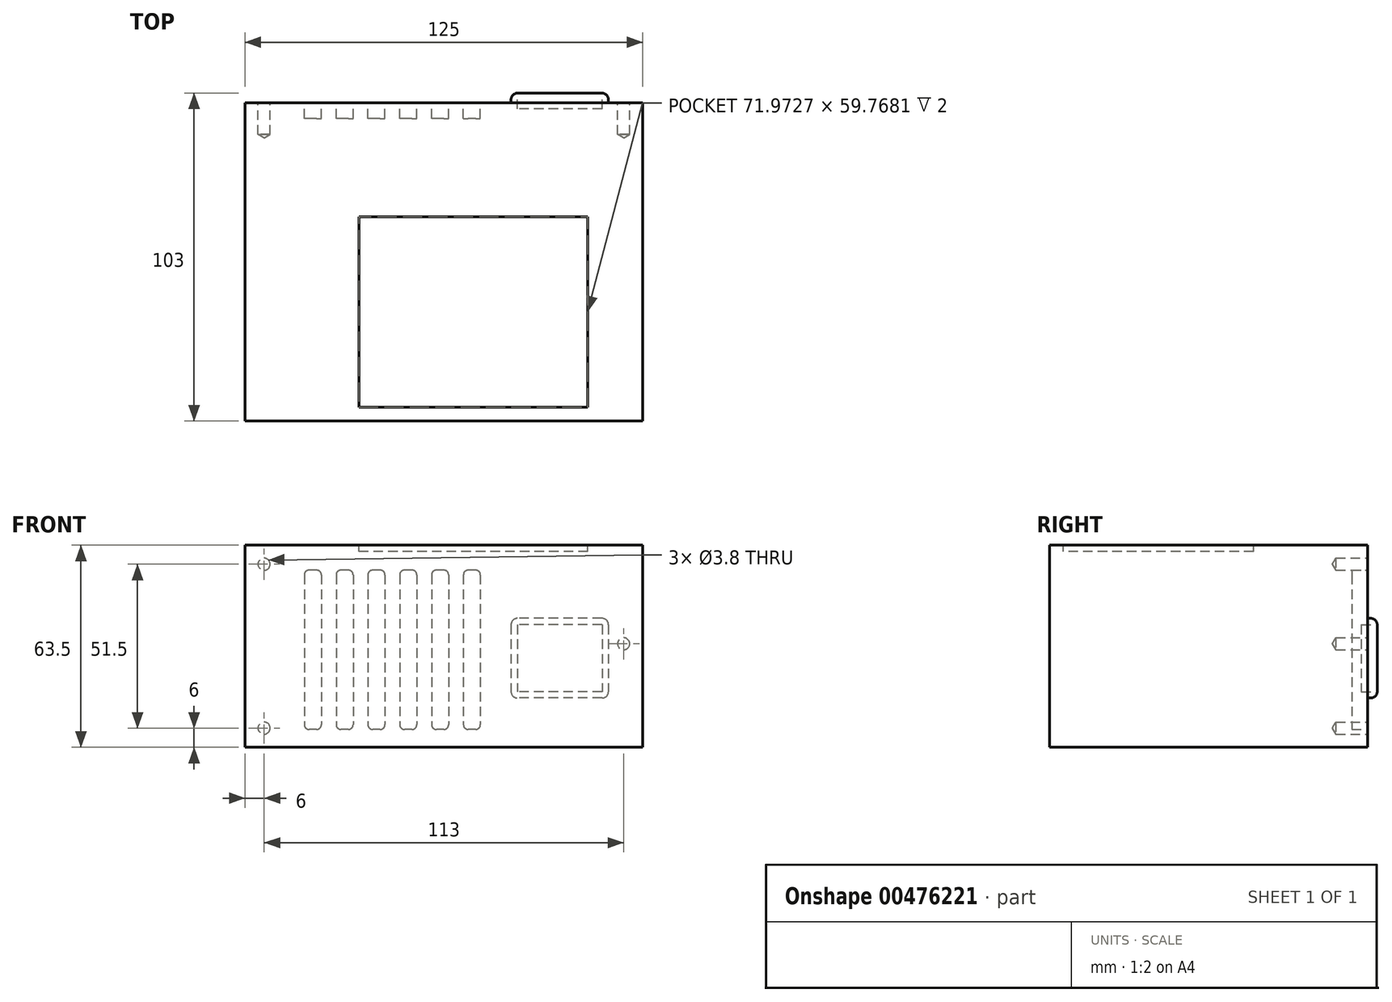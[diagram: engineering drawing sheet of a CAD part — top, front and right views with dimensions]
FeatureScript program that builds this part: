
annotation { "Feature Type Name" : "Feature", "Feature Type Description" : "" }
export const myFeature = defineFeature(function(context is Context, id is Id, definition is map)
    precondition{}
    {
        {
            var Q0;
            Q0=qCreatedBy(makeId("Top.planeOp"),FACE);
            var sketch = newSketch(context, id + "F0", { "sketchPlane" : qUnion([Q0])});
            skLineSegment(sketch, "E0.bottom", {"start": v(62.5, -50) * mm, "end": v(-62.5, -50) * mm});
            skLineSegment(sketch, "E0.top", {"start": v(62.5, 50) * mm, "end": v(-62.5, 50) * mm});
            skLineSegment(sketch, "E0.left", {"start": v(62.5, -50) * mm, "end": v(62.5, 50) * mm});
            skLineSegment(sketch, "E0.right", {"start": v(-62.5, -50) * mm, "end": v(-62.5, 50) * mm});
            skPoint(sketch, "E0.middle", {"position": v(0, 0) * mm});
            skSolve(sketch);
        }
        {
            var Q0;
            Q0=makeQuery(id+"F0.imprint","IMPRINT",FACE,{"disambiguationData":[TD([[makeQuery(id+"F0.imprint","IMPRINT",EDGE,{"derivedFrom":sQuery(id+"F0.wireOp",EDGE,"E0.bottom")}),-1.0]])]});
            extrude(context, id + "F1", {"entities" : qUnion([Q0]), "depth" : 63.5 * mm});
        }
        {
            var Q0;
            Q0=makeQuery(id+"F1.opExtrude","SWEPT_FACE",FACE,{"disambiguationData":[OSD([sQuery(id+"F0.wireOp",EDGE,"E0.top")])]});
            var sketch = newSketch(context, id + "F2", { "sketchPlane" : qUnion([Q0])});
            skPoint(sketch, "E1", {"position": v(56.5, 6) * mm});
            skPoint(sketch, "E2", {"position": v(56.5, 57.5) * mm});
            skPoint(sketch, "E3", {"position": v(-56.5, 32.5) * mm});
            skLineSegment(sketch, "E4.bottom", {"start": v(-51.73, 40.5) * mm, "end": v(-21.11, 40.5) * mm});
            skLineSegment(sketch, "E4.top", {"start": v(-51.73, 15.46) * mm, "end": v(-21.11, 15.46) * mm});
            skLineSegment(sketch, "E4.left", {"start": v(-51.73, 40.5) * mm, "end": v(-51.73, 15.46) * mm});
            skLineSegment(sketch, "E4.right", {"start": v(-21.11, 40.5) * mm, "end": v(-21.11, 15.46) * mm});
            skSolve(sketch);
        }
        {
            var Q0;
            Q0=sQuery(id+"F2.wireOp",VERTEX,"E3");
            var Q1;
            Q1=sQuery(id+"F2.wireOp",VERTEX,"E2");
            var Q2;
            Q2=sQuery(id+"F2.wireOp",VERTEX,"E1");
            var Q3;
            Q3=makeQuery(id+"F1.opExtrude","SWEPT_BODY",BODY,{"disambiguationData":[OSD([sQuery(id+"F0.wireOp",EDGE,"E0.bottom"),sQuery(id+"F0.wireOp",EDGE,"E0.top"),sQuery(id+"F0.wireOp",EDGE,"E0.left"),sQuery(id+"F0.wireOp",EDGE,"E0.right")])]});
            hole(context, id + "F3", {"style" : HoleStyle.SIMPLE, "endStyle" : HoleEndStyle.BLIND, "standardTappedOrClearance" : lookupTablePath({ "standard" : "ANSI", "fit" : "Normal (ASME)", "size" : "#6", "type" : "Clearance" }), "standardBlindInLast" : lookupTablePath({ "fit" : "Free", "standard" : "ANSI", "size" : "#6", "type" : "Clearance" }), "holeDiameter" : 3.8 * mm, "holeDepth" : 10 * mm, "isTappedThrough" : true, "tappedDepth" : 3.8 * mm, "tapClearance" : 0, "locations" : qUnion([Q0, Q1, Q2]), "scope" : qUnion([Q3])});
        }
        {
            var Q0;
            Q0=makeQuery(id+"F2.imprint","IMPRINT",FACE,{"disambiguationData":[TD([[makeQuery(id+"F2.imprint","IMPRINT",EDGE,{"derivedFrom":sQuery(id+"F2.wireOp",EDGE,"E4.bottom")}),-1.0]])]});
            extrude(context, id + "F4", {"entities" : qUnion([Q0]), "operationType" : NewBodyOperationType.ADD, "depth" : 3 * mm});
        }
        {
            var Q0;
            Q0=makeQuery(id+"F4.opExtrude","CAP_FACE",FACE,{"disambiguationData":[OSD([sQuery(id+"F2.wireOp",EDGE,"E4.bottom"),sQuery(id+"F2.wireOp",EDGE,"E4.top"),sQuery(id+"F2.wireOp",EDGE,"E4.left"),sQuery(id+"F2.wireOp",EDGE,"E4.right")])],"isStart":false});
            var Q1;
            Q1=makeQuery(id+"F4.opExtrude","SWEPT_EDGE",EDGE,{"disambiguationData":[OSD([sQuery(id+"F2.wireOp",EDGE,"E4.bottom"),sQuery(id+"F2.wireOp",EDGE,"E4.right")])]});
            var Q2;
            Q2=makeQuery(id+"F4.opExtrude","SWEPT_EDGE",EDGE,{"disambiguationData":[OSD([sQuery(id+"F2.wireOp",EDGE,"E4.top"),sQuery(id+"F2.wireOp",EDGE,"E4.right")])]});
            var Q3;
            Q3=makeQuery(id+"F4.opExtrude","SWEPT_EDGE",EDGE,{"disambiguationData":[OSD([sQuery(id+"F2.wireOp",EDGE,"E4.bottom"),sQuery(id+"F2.wireOp",EDGE,"E4.left")])]});
            var Q4;
            Q4=makeQuery(id+"F4.opExtrude","SWEPT_EDGE",EDGE,{"disambiguationData":[OSD([sQuery(id+"F2.wireOp",EDGE,"E4.top"),sQuery(id+"F2.wireOp",EDGE,"E4.left")])]});
            fillet(context, id + "F5", {"entities" : qUnion([Q0, Q1, Q2, Q3, Q4]), "radius" : 2 * mm, "tangentPropagation" : true, "allowEdgeOverflow" : false});
        }
        {
            var Q0;
            Q0=makeQuery(id+"F1.opExtrude","CAP_FACE",FACE,{"disambiguationData":[OSD([sQuery(id+"F0.wireOp",EDGE,"E0.bottom"),sQuery(id+"F0.wireOp",EDGE,"E0.top"),sQuery(id+"F0.wireOp",EDGE,"E0.left"),sQuery(id+"F0.wireOp",EDGE,"E0.right")])],"isStart":false});
            var sketch = newSketch(context, id + "F6", { "sketchPlane" : qUnion([Q0])});
            skLineSegment(sketch, "E5.bottom", {"start": v(45.26, 14.14) * mm, "end": v(-26.71, 14.14) * mm});
            skLineSegment(sketch, "E5.top", {"start": v(45.26, -45.63) * mm, "end": v(-26.71, -45.63) * mm});
            skLineSegment(sketch, "E5.left", {"start": v(45.26, 14.14) * mm, "end": v(45.26, -45.63) * mm});
            skLineSegment(sketch, "E5.right", {"start": v(-26.71, 14.14) * mm, "end": v(-26.71, -45.63) * mm});
            skSolve(sketch);
        }
        {
            var Q0;
            Q0=makeQuery(id+"F6.imprint","IMPRINT",FACE,{"disambiguationData":[TD([[makeQuery(id+"F6.imprint","IMPRINT",EDGE,{"derivedFrom":sQuery(id+"F6.wireOp",EDGE,"E5.bottom")}),1.0]])]});
            extrude(context, id + "F7", {"entities" : qUnion([Q0]), "operationType" : NewBodyOperationType.REMOVE, "oppositeDirection" : true, "depth" : 2 * mm});
        }
        {
            var Q0;
            Q0=makeQuery(id+"F1.opExtrude","SWEPT_FACE",FACE,{"disambiguationData":[OSD([sQuery(id+"F0.wireOp",EDGE,"E0.top")])]});
            var sketch = newSketch(context, id + "F8", { "sketchPlane" : qUnion([Q0])});
            skLineSegment(sketch, "E6.bottom", {"start": v(-9.99, 55.64) * mm, "end": v(-7.65, 55.64) * mm});
            skLineSegment(sketch, "E6.top", {"start": v(-9.99, 5.58) * mm, "end": v(-7.65, 5.58) * mm});
            skLineSegment(sketch, "E6.left", {"start": v(-11.49, 54.14) * mm, "end": v(-11.49, 7.08) * mm});
            skLineSegment(sketch, "E6.right", {"start": v(-6.15, 54.14) * mm, "end": v(-6.15, 7.08) * mm});
            skPoint(sketch, "E7.visualSharp", {"position": v(-11.49, 55.64) * mm});
            skArc(sketch, "E7.filletArc", {"start": v(-9.99, 55.64) * mm, "mid": v(-11.05, 55.2) * mm, "end": v(-11.49, 54.14) * mm});
            skPoint(sketch, "E8.visualSharp", {"position": v(-6.15, 55.64) * mm});
            skArc(sketch, "E8.filletArc", {"start": v(-6.15, 54.14) * mm, "mid": v(-6.59, 55.2) * mm, "end": v(-7.65, 55.64) * mm});
            skPoint(sketch, "E9.visualSharp", {"position": v(-6.15, 5.58) * mm});
            skArc(sketch, "E9.filletArc", {"start": v(-7.65, 5.58) * mm, "mid": v(-6.59, 6.02) * mm, "end": v(-6.15, 7.08) * mm});
            skPoint(sketch, "E10.visualSharp", {"position": v(-11.49, 5.58) * mm});
            skArc(sketch, "E10.filletArc", {"start": v(-11.49, 7.08) * mm, "mid": v(-11.05, 6.02) * mm, "end": v(-9.99, 5.58) * mm});
            skLineSegment(sketch, "E11.1.0.0", {"start": v(0.01, 55.64) * mm, "end": v(2.35, 55.64) * mm});
            skPoint(sketch, "E11.1.0.1", {"position": v(3.85, 55.64) * mm});
            skArc(sketch, "E11.1.0.2", {"start": v(3.85, 54.14) * mm, "mid": v(3.41, 55.2) * mm, "end": v(2.35, 55.64) * mm});
            skLineSegment(sketch, "E11.1.0.3", {"start": v(3.85, 54.14) * mm, "end": v(3.85, 7.08) * mm});
            skArc(sketch, "E11.1.0.4", {"start": v(2.35, 5.58) * mm, "mid": v(3.41, 6.02) * mm, "end": v(3.85, 7.08) * mm});
            skLineSegment(sketch, "E11.1.0.5", {"start": v(0.01, 5.58) * mm, "end": v(2.35, 5.58) * mm});
            skArc(sketch, "E11.1.0.6", {"start": v(-1.49, 7.08) * mm, "mid": v(-1.05, 6.02) * mm, "end": v(0.01, 5.58) * mm});
            skLineSegment(sketch, "E11.1.0.7", {"start": v(-1.49, 54.14) * mm, "end": v(-1.49, 7.08) * mm});
            skArc(sketch, "E11.1.0.8", {"start": v(0.01, 55.64) * mm, "mid": v(-1.05, 55.2) * mm, "end": v(-1.49, 54.14) * mm});
            skLineSegment(sketch, "E11.2.0.0", {"start": v(10.01, 55.64) * mm, "end": v(12.35, 55.64) * mm});
            skPoint(sketch, "E11.2.0.1", {"position": v(13.85, 55.64) * mm});
            skArc(sketch, "E11.2.0.2", {"start": v(13.85, 54.14) * mm, "mid": v(13.41, 55.2) * mm, "end": v(12.35, 55.64) * mm});
            skLineSegment(sketch, "E11.2.0.3", {"start": v(13.85, 54.14) * mm, "end": v(13.85, 7.08) * mm});
            skArc(sketch, "E11.2.0.4", {"start": v(12.35, 5.58) * mm, "mid": v(13.41, 6.02) * mm, "end": v(13.85, 7.08) * mm});
            skLineSegment(sketch, "E11.2.0.5", {"start": v(10.01, 5.58) * mm, "end": v(12.35, 5.58) * mm});
            skArc(sketch, "E11.2.0.6", {"start": v(8.51, 7.08) * mm, "mid": v(8.95, 6.02) * mm, "end": v(10.01, 5.58) * mm});
            skLineSegment(sketch, "E11.2.0.7", {"start": v(8.51, 54.14) * mm, "end": v(8.51, 7.08) * mm});
            skArc(sketch, "E11.2.0.8", {"start": v(10.01, 55.64) * mm, "mid": v(8.95, 55.2) * mm, "end": v(8.51, 54.14) * mm});
            skLineSegment(sketch, "E11.3.0.0", {"start": v(20.01, 55.64) * mm, "end": v(22.35, 55.64) * mm});
            skPoint(sketch, "E11.3.0.1", {"position": v(23.85, 55.64) * mm});
            skArc(sketch, "E11.3.0.2", {"start": v(23.85, 54.14) * mm, "mid": v(23.41, 55.2) * mm, "end": v(22.35, 55.64) * mm});
            skLineSegment(sketch, "E11.3.0.3", {"start": v(23.85, 54.14) * mm, "end": v(23.85, 7.08) * mm});
            skArc(sketch, "E11.3.0.4", {"start": v(22.35, 5.58) * mm, "mid": v(23.41, 6.02) * mm, "end": v(23.85, 7.08) * mm});
            skLineSegment(sketch, "E11.3.0.5", {"start": v(20.01, 5.58) * mm, "end": v(22.35, 5.58) * mm});
            skArc(sketch, "E11.3.0.6", {"start": v(18.51, 7.08) * mm, "mid": v(18.95, 6.02) * mm, "end": v(20.01, 5.58) * mm});
            skLineSegment(sketch, "E11.3.0.7", {"start": v(18.51, 54.14) * mm, "end": v(18.51, 7.08) * mm});
            skArc(sketch, "E11.3.0.8", {"start": v(20.01, 55.64) * mm, "mid": v(18.95, 55.2) * mm, "end": v(18.51, 54.14) * mm});
            skLineSegment(sketch, "E11.4.0.0", {"start": v(30.01, 55.64) * mm, "end": v(32.35, 55.64) * mm});
            skPoint(sketch, "E11.4.0.1", {"position": v(33.85, 55.64) * mm});
            skArc(sketch, "E11.4.0.2", {"start": v(33.85, 54.14) * mm, "mid": v(33.41, 55.2) * mm, "end": v(32.35, 55.64) * mm});
            skLineSegment(sketch, "E11.4.0.3", {"start": v(33.85, 54.14) * mm, "end": v(33.85, 7.08) * mm});
            skArc(sketch, "E11.4.0.4", {"start": v(32.35, 5.58) * mm, "mid": v(33.41, 6.02) * mm, "end": v(33.85, 7.08) * mm});
            skLineSegment(sketch, "E11.4.0.5", {"start": v(30.01, 5.58) * mm, "end": v(32.35, 5.58) * mm});
            skArc(sketch, "E11.4.0.6", {"start": v(28.51, 7.08) * mm, "mid": v(28.95, 6.02) * mm, "end": v(30.01, 5.58) * mm});
            skLineSegment(sketch, "E11.4.0.7", {"start": v(28.51, 54.14) * mm, "end": v(28.51, 7.08) * mm});
            skArc(sketch, "E11.4.0.8", {"start": v(30.01, 55.64) * mm, "mid": v(28.95, 55.2) * mm, "end": v(28.51, 54.14) * mm});
            skLineSegment(sketch, "E11.5.0.0", {"start": v(40.01, 55.64) * mm, "end": v(42.35, 55.64) * mm});
            skPoint(sketch, "E11.5.0.1", {"position": v(43.85, 55.64) * mm});
            skArc(sketch, "E11.5.0.2", {"start": v(43.85, 54.14) * mm, "mid": v(43.41, 55.2) * mm, "end": v(42.35, 55.64) * mm});
            skLineSegment(sketch, "E11.5.0.3", {"start": v(43.85, 54.14) * mm, "end": v(43.85, 7.08) * mm});
            skArc(sketch, "E11.5.0.4", {"start": v(42.35, 5.58) * mm, "mid": v(43.41, 6.02) * mm, "end": v(43.85, 7.08) * mm});
            skLineSegment(sketch, "E11.5.0.5", {"start": v(40.01, 5.58) * mm, "end": v(42.35, 5.58) * mm});
            skArc(sketch, "E11.5.0.6", {"start": v(38.51, 7.08) * mm, "mid": v(38.95, 6.02) * mm, "end": v(40.01, 5.58) * mm});
            skLineSegment(sketch, "E11.5.0.7", {"start": v(38.51, 54.14) * mm, "end": v(38.51, 7.08) * mm});
            skArc(sketch, "E11.5.0.8", {"start": v(40.01, 55.64) * mm, "mid": v(38.95, 55.2) * mm, "end": v(38.51, 54.14) * mm});
            skLineSegment(sketch, "E11.direction1", {"start": v(-9.99, 55.64) * mm, "end": v(0.01, 55.64) * mm, "construction": true});
            skSolve(sketch);
        }
        {
            var Q0;
            Q0=makeQuery(id+"F8.imprint","IMPRINT",FACE,{"disambiguationData":[TD([[makeQuery(id+"F8.imprint","IMPRINT",EDGE,{"derivedFrom":sQuery(id+"F8.wireOp",EDGE,"E6.bottom")}),-1.0]])]});
            var Q1;
            Q1=makeQuery(id+"F8.imprint","IMPRINT",FACE,{"disambiguationData":[TD([[makeQuery(id+"F8.imprint","IMPRINT",EDGE,{"derivedFrom":sQuery(id+"F8.wireOp",EDGE,"E11.1.0.0")}),-1.0]])]});
            var Q2;
            Q2=makeQuery(id+"F8.imprint","IMPRINT",FACE,{"disambiguationData":[TD([[makeQuery(id+"F8.imprint","IMPRINT",EDGE,{"derivedFrom":sQuery(id+"F8.wireOp",EDGE,"E11.2.0.0")}),-1.0]])]});
            var Q3;
            Q3=makeQuery(id+"F8.imprint","IMPRINT",FACE,{"disambiguationData":[TD([[makeQuery(id+"F8.imprint","IMPRINT",EDGE,{"derivedFrom":sQuery(id+"F8.wireOp",EDGE,"E11.3.0.0")}),-1.0]])]});
            var Q4;
            Q4=makeQuery(id+"F8.imprint","IMPRINT",FACE,{"disambiguationData":[TD([[makeQuery(id+"F8.imprint","IMPRINT",EDGE,{"derivedFrom":sQuery(id+"F8.wireOp",EDGE,"E11.4.0.0")}),-1.0]])]});
            var Q5;
            Q5=makeQuery(id+"F8.imprint","IMPRINT",FACE,{"disambiguationData":[TD([[makeQuery(id+"F8.imprint","IMPRINT",EDGE,{"derivedFrom":sQuery(id+"F8.wireOp",EDGE,"E11.5.0.0")}),-1.0]])]});
            extrude(context, id + "F9", {"entities" : qUnion([Q0, Q1, Q2, Q3, Q4, Q5]), "operationType" : NewBodyOperationType.REMOVE, "oppositeDirection" : true, "depth" : 5 * mm});
        }
        {
            var Q0;
            Q0=makeQuery(id+"F4.opExtrude","CAP_FACE",FACE,{"disambiguationData":[OSD([sQuery(id+"F2.wireOp",EDGE,"E4.bottom"),sQuery(id+"F2.wireOp",EDGE,"E4.top"),sQuery(id+"F2.wireOp",EDGE,"E4.left"),sQuery(id+"F2.wireOp",EDGE,"E4.right")])],"isStart":false});
            extrude(context, id + "F10", {"entities" : qUnion([Q0]), "operationType" : NewBodyOperationType.REMOVE, "oppositeDirection" : true, "depth" : 5 * mm});
        }
    });
